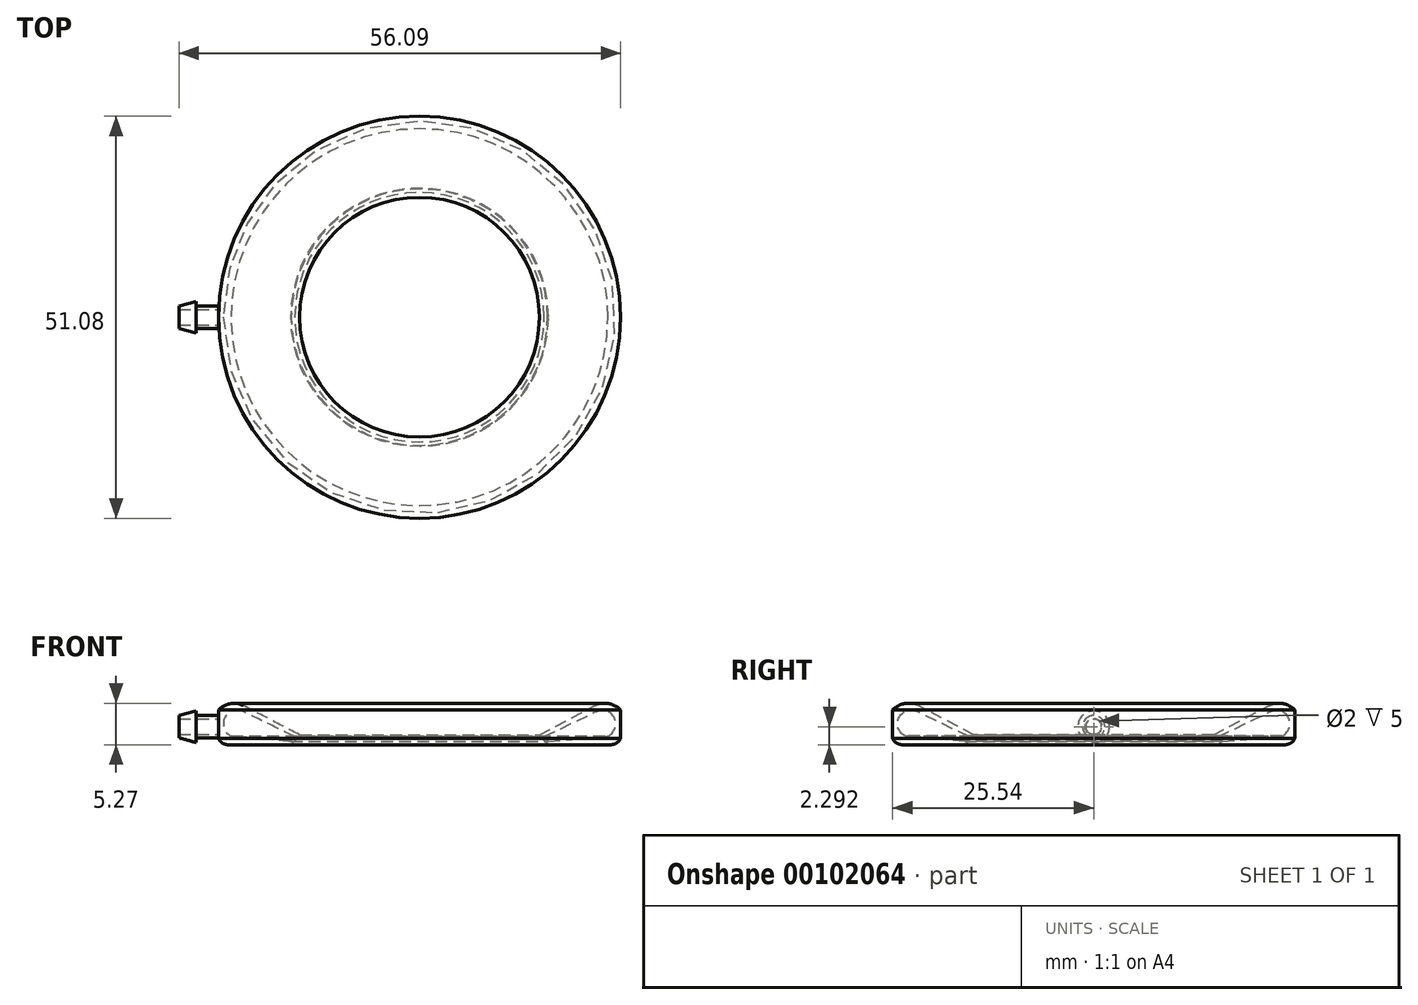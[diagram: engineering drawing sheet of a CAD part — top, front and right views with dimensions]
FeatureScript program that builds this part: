
annotation { "Feature Type Name" : "Feature", "Feature Type Description" : "" }
export const myFeature = defineFeature(function(context is Context, id is Id, definition is map)
    precondition{}
    {
        {
            var Q0;
            Q0=qCreatedBy(makeId("Front.planeOp"),FACE);
            var sketch = newSketch(context, id + "F0", { "sketchPlane" : qUnion([Q0])});
            skLineSegment(sketch, "E0", {"start": v(15, 0) * mm, "end": v(16.29, 0) * mm});
            skLineSegment(sketch, "E1", {"start": v(15.23, 1.25) * mm, "end": v(22.32, 4.96) * mm});
            skLineSegment(sketch, "E2", {"start": v(16.29, 0) * mm, "end": v(24.29, 0) * mm});
            skLineSegment(sketch, "E3", {"start": v(15.53, 0.9) * mm, "end": v(22.43, 4.22) * mm});
            skLineSegment(sketch, "E4", {"start": v(15.97, 0.38) * mm, "end": v(23.94, 1.1) * mm});
            skArc(sketch, "E5", {"start": v(23.94, 1.1) * mm, "mid": v(24.74, 3.4) * mm, "end": v(22.43, 4.22) * mm});
            skLineSegment(sketch, "E6", {"start": v(0, 0) * mm, "end": v(0, 3.69) * mm});
            skLineSegment(sketch, "E7", {"start": v(15.53, 0.9) * mm, "end": v(15.23, 1.25) * mm});
            skLineSegment(sketch, "E8", {"start": v(15.97, 0.38) * mm, "end": v(16.29, 0) * mm});
            skLineSegment(sketch, "E9", {"start": v(25.54, 4.4) * mm, "end": v(25.54, 0.77) * mm});
            skArc(sketch, "E10", {"start": v(25.54, 4.4) * mm, "mid": v(24.03, 5.23) * mm, "end": v(22.32, 4.96) * mm});
            skArc(sketch, "E11", {"start": v(24.29, 0) * mm, "mid": v(25.02, 0.2) * mm, "end": v(25.54, 0.77) * mm});
            skLineSegment(sketch, "E12", {"start": v(15.49, 0.95) * mm, "end": v(15.97, 0.38) * mm});
            skLineSegment(sketch, "E13", {"start": v(16.37, 0.41) * mm, "end": v(15.84, 1.04) * mm});
            skSolve(sketch);
        }
        {
            var Q0;
            {var subQ0=sQuery(id+"F0.wireOp",EDGE,"E1");Q0=makeQuery(id+"F0.imprint","IMPRINT",FACE,{"disambiguationData":[TD([[makeQuery(id+"F0.imprint","IMPRINT",EDGE,{"derivedFrom":subQ0}),-1.0]])]});}
            var Q1;
            {var subQ5=sQuery(id+"F0.wireOp",EDGE,"URcUcSot-s3Vu-5bZ4-lVOO-fd6WexAXXO60");Q1=makeQuery(id+"F0.imprint","IMPRINT",FACE,{"disambiguationData":[TD([[makeQuery(id+"F0.imprint","IMPRINT",EDGE,{"derivedFrom":subQ5}),-1.0]])]});}
            var Q2;
            {var subQ3=sQuery(id+"F0.wireOp",EDGE,"E13");Q2=makeQuery(id+"F0.imprint","IMPRINT",FACE,{"disambiguationData":[TD([[makeQuery(id+"F0.imprint","IMPRINT",EDGE,{"derivedFrom":subQ3}),1.0]])]});}
            var Q3;
            Q3=sQuery(id+"F0.wireOp",EDGE,"E6");
            revolve(context, id + "F1", {"entities" : qUnion([Q0, Q1, Q2]), "axis" : qUnion([Q3]), "revolveType" : RevolveType.FULL});
        }
        {
            var Q0;
            Q0=qCreatedBy(makeId("Front.planeOp"),FACE);
            var sketch = newSketch(context, id + "F2", { "sketchPlane" : qUnion([Q0])});
            skLineSegment(sketch, "E14", {"start": v(-25.54, 2.3) * mm, "end": v(-27.05, 2.3) * mm});
            skLineSegment(sketch, "E15", {"start": v(-28.4, 3.7) * mm, "end": v(-28.4, 4.3) * mm});
            skLineSegment(sketch, "E16", {"start": v(-28.4, 4.3) * mm, "end": v(-30.55, 3.7) * mm});
            skLineSegment(sketch, "E17", {"start": v(-30.55, 3.7) * mm, "end": v(-30.55, 3.3) * mm});
            skLineSegment(sketch, "E18", {"start": v(-30.55, 3.3) * mm, "end": v(-25.55, 3.3) * mm});
            skLineSegment(sketch, "E19", {"start": v(-25.55, 3.3) * mm, "end": v(-25.4, 3.7) * mm});
            skLineSegment(sketch, "E20", {"start": v(-25.4, 3.7) * mm, "end": v(-28.4, 3.7) * mm});
            skSolve(sketch);
        }
        {
            var Q0;
            Q0 = qSketchRegion(id + "F2", true);
            var Q1;
            Q1=sQuery(id+"F2.wireOp",EDGE,"E14");
            revolve(context, id + "F3", {"operationType" : NewBodyOperationType.ADD, "entities" : qUnion([Q0]), "axis" : qUnion([Q1]), "revolveType" : RevolveType.FULL});
        }
    });
